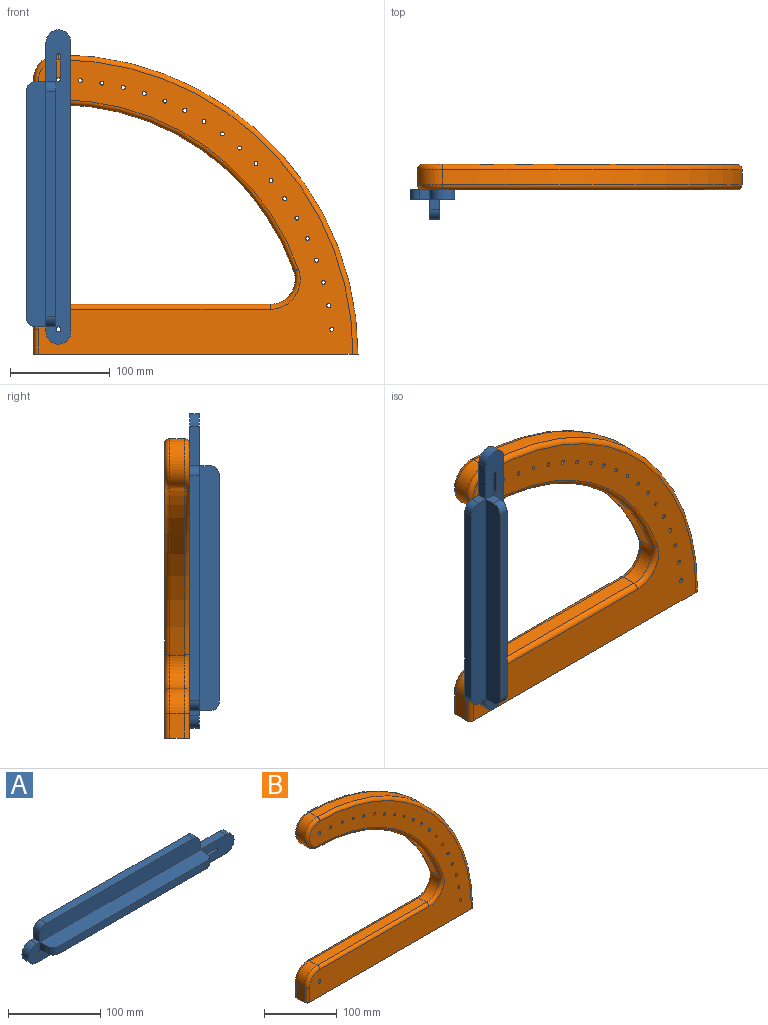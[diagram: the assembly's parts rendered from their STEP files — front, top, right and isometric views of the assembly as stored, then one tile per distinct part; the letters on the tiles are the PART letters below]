
ASSEMBLY  parts=2 mates=1
PART A: 25 faces, bbox 315x30x45 mm
  f0: plane 39.5x10mm, normal (0,0,1), area 395mm2, adj f2,f10,f12,f19
  f1: plane 245.5x20mm, normal (0,0,1), area 4867.1mm2, adj f13,f14,f16,f18,f23,f24
  f2: plane 315x25mm, normal (0,-1,0), area 5158.2mm2, adj f0,f3,f4,f5,f6,f7,f8,f9
  f3: plane 290x10mm, normal (0,0,-1), area 2900mm2, adj f2,f10,f11,f12
  f4: cylinder r=2mm len=10mm, axis (0,1,0), area 62.8mm2, adj f2,f5,f7,f10
  f5: plane 23.86x10mm, normal (0,0,-1), area 238.6mm2, adj f2,f4,f6,f10
  f6: cylinder r=2mm len=10mm, axis (0,1,0), area 62.8mm2, adj f2,f5,f7,f10
  f7: plane 23.86x10mm, normal (0,0,1), area 238.6mm2, adj f2,f4,f6,f10
  f8: cylinder r=2.5mm len=10mm, axis (0,1,0), area 157.1mm2, adj f2,f10
  f9: plane 10x5mm, normal (0,0,1), area 50mm2, adj f2,f10,f11,f17
  f10: plane 315x45mm, normal (0,1,0), area 12480.3mm2, adj f0,f3,f4,f5,f6,f7,f8,f9
  f11: cylinder r=12.5mm len=25mm, axis (0,1,0), area 392.7mm2, adj f2,f3,f9,f10
  f12: cylinder r=12.5mm len=25mm, axis (0,-1,0), area 392.7mm2, adj f0,f2,f3,f10
  f13: plane 10x10mm, normal (1,0,0), area 100mm2, adj f1,f2,f15,f24
  f14: plane 10x10mm, normal (-1,0,0), area 100mm2, adj f1,f2,f15,f23
  f15: plane 245.5x20mm, normal (0,0,-1), area 4867.1mm2, adj f2,f13,f14,f16,f23,f24
  f16: plane 225.5x10mm, normal (0,-1,0), area 2255mm2, adj f1,f15,f23,f24
  f17: plane 10x10mm, normal (-1,0,0), area 100mm2, adj f9,f10,f18,f21
  f18: plane 245.5x20mm, normal (0,-1,0), area 4867.1mm2, adj f1,f17,f19,f20,f21,f22
  f19: plane 10x10mm, normal (1,0,0), area 100mm2, adj f0,f10,f18,f22
  f20: plane 225.5x10mm, normal (0,0,1), area 2255mm2, adj f10,f18,f21,f22
  f21: cylinder r=10mm len=10mm, axis (0,1,0), area 157.1mm2, adj f10,f17,f18,f20
  f22: cylinder r=10mm len=10mm, axis (0,-1,0), area 157.1mm2, adj f10,f18,f19,f20
  f23: cylinder r=10mm len=10mm, axis (0,0,1), area 157.1mm2, adj f1,f14,f15,f16
  f24: cylinder r=10mm len=10mm, axis (0,0,-1), area 157.1mm2, adj f1,f13,f15,f16
PART B: 44 faces, bbox 351.8x25x324.7 mm
  f0: plane 315x295mm, normal (0,-1,0), area 30243mm2, adj f5,f8,f9,f10,f11,f12,f13,f14
  f1: plane 315x295mm, normal (0,1,0), area 30243mm2, adj f5,f8,f9,f10,f11,f12,f13,f14
  f2: cylinder r=25mm len=33.33mm, axis (0,1,0), area 716.5mm2, adj f3,f28,f31,f37
  f3: plane 212.13x15mm, normal (0,0,1), area 3182mm2, adj f2,f30,f36,f42
  f4: plane 25x15mm, normal (-1,0,0), area 375mm2, adj f5,f29,f35,f42
  f5: plane 325x25mm, normal (0,0,-1), area 8103.5mm2, adj f0,f1,f4,f6,f29,f34,f35,f40
  f6: cylinder r=300mm len=300mm, axis (0,1,0), area 7068.6mm2, adj f5,f7,f34,f40
  f7: cylinder r=25mm len=50mm, axis (0,1,0), area 1178.1mm2, adj f6,f28,f33,f39
  f8: cylinder r=2mm len=25mm, axis (0,1,0), area 314.2mm2, adj f0,f1
  f9: cylinder r=2mm len=25mm, axis (0,1,0), area 314.2mm2, adj f0,f1
  f10: cylinder r=2mm len=25mm, axis (0,1,0), area 314.2mm2, adj f0,f1
  f11: cylinder r=2mm len=25mm, axis (0,1,0), area 314.2mm2, adj f0,f1
  f12: cylinder r=2mm len=25mm, axis (0,1,0), area 314.2mm2, adj f0,f1
  f13: cylinder r=2mm len=25mm, axis (0,1,0), area 314.2mm2, adj f0,f1
  f14: cylinder r=2mm len=25mm, axis (0,1,0), area 314.2mm2, adj f0,f1
  f15: cylinder r=2mm len=25mm, axis (0,1,0), area 314.2mm2, adj f0,f1
  f16: cylinder r=2mm len=25mm, axis (0,1,0), area 314.2mm2, adj f0,f1
  f17: cylinder r=2mm len=25mm, axis (0,1,0), area 314.2mm2, adj f0,f1
  f18: cylinder r=2mm len=25mm, axis (0,1,0), area 314.2mm2, adj f0,f1
  f19: cylinder r=2mm len=25mm, axis (0,1,0), area 314.2mm2, adj f0,f1
  f20: cylinder r=2mm len=25mm, axis (0,1,0), area 314.2mm2, adj f0,f1
  f21: cylinder r=2mm len=25mm, axis (0,1,0), area 314.2mm2, adj f0,f1
  f22: cylinder r=2mm len=25mm, axis (0,1,0), area 314.2mm2, adj f0,f1
  f23: cylinder r=2mm len=25mm, axis (0,1,0), area 314.2mm2, adj f0,f1
  f24: cylinder r=2mm len=25mm, axis (0,1,0), area 314.2mm2, adj f0,f1
  f25: cylinder r=2mm len=25mm, axis (0,1,0), area 314.2mm2, adj f0,f1
  f26: cylinder r=2.5mm len=25mm, axis (0,1,0), area 392.7mm2, adj f0,f1
  f27: cylinder r=2mm len=25mm, axis (0,1,0), area 314.2mm2, adj f0,f1
  f28: cylinder r=250mm len=235.7mm, axis (0,1,0), area 4616.1mm2, adj f2,f7,f32,f38
  f29: cylinder r=5mm len=25mm, axis (0,0,-1), area 196.3mm2, adj f1,f4,f5,f43
  f30: cylinder r=5mm len=212.13mm, axis (-1,0,0), area 1666.1mm2, adj f1,f3,f31,f43
  f31: torus R=30mm, axis (0,-1,0), area 402.4mm2, adj f1,f2,f30,f32
  f32: torus R=255mm, axis (0,-1,0), area 2434.6mm2, adj f1,f28,f31,f33
  f33: torus R=20mm, axis (0,-1,0), area 572mm2, adj f1,f7,f32,f34
  f34: torus R=295mm, axis (0,-1,0), area 3678.7mm2, adj f1,f5,f6,f33
  f35: cylinder r=5mm len=25mm, axis (0,0,1), area 196.3mm2, adj f0,f4,f5,f41
  f36: cylinder r=5mm len=212.13mm, axis (1,0,0), area 1666.1mm2, adj f0,f3,f37,f41
  f37: torus R=30mm, axis (0,-1,0), area 402.4mm2, adj f0,f2,f36,f38
  f38: torus R=255mm, axis (0,-1,0), area 2434.6mm2, adj f0,f28,f37,f39
  f39: torus R=20mm, axis (0,-1,0), area 572mm2, adj f0,f7,f38,f40
  f40: torus R=295mm, axis (0,-1,0), area 3678.7mm2, adj f0,f5,f6,f39
  f41: torus R=20mm, axis (0,-1,0), area 286mm2, adj f0,f35,f36,f42
  f42: cylinder r=25mm len=25mm, axis (0,-1,0), area 589mm2, adj f3,f4,f41,f43
  f43: torus R=20mm, axis (0,-1,0), area 286mm2, adj f1,f29,f30,f42
PLACE A rot(axis=(0,-1,0),90deg) t=(-182.47,73.49,78.88)mm
PLACE B t=(-194.97,98.49,78.88)mm
MATE revolute A.f8 <-> B.f26  axis (0,1,0) through (-194.97,73.49,103.88)mm
